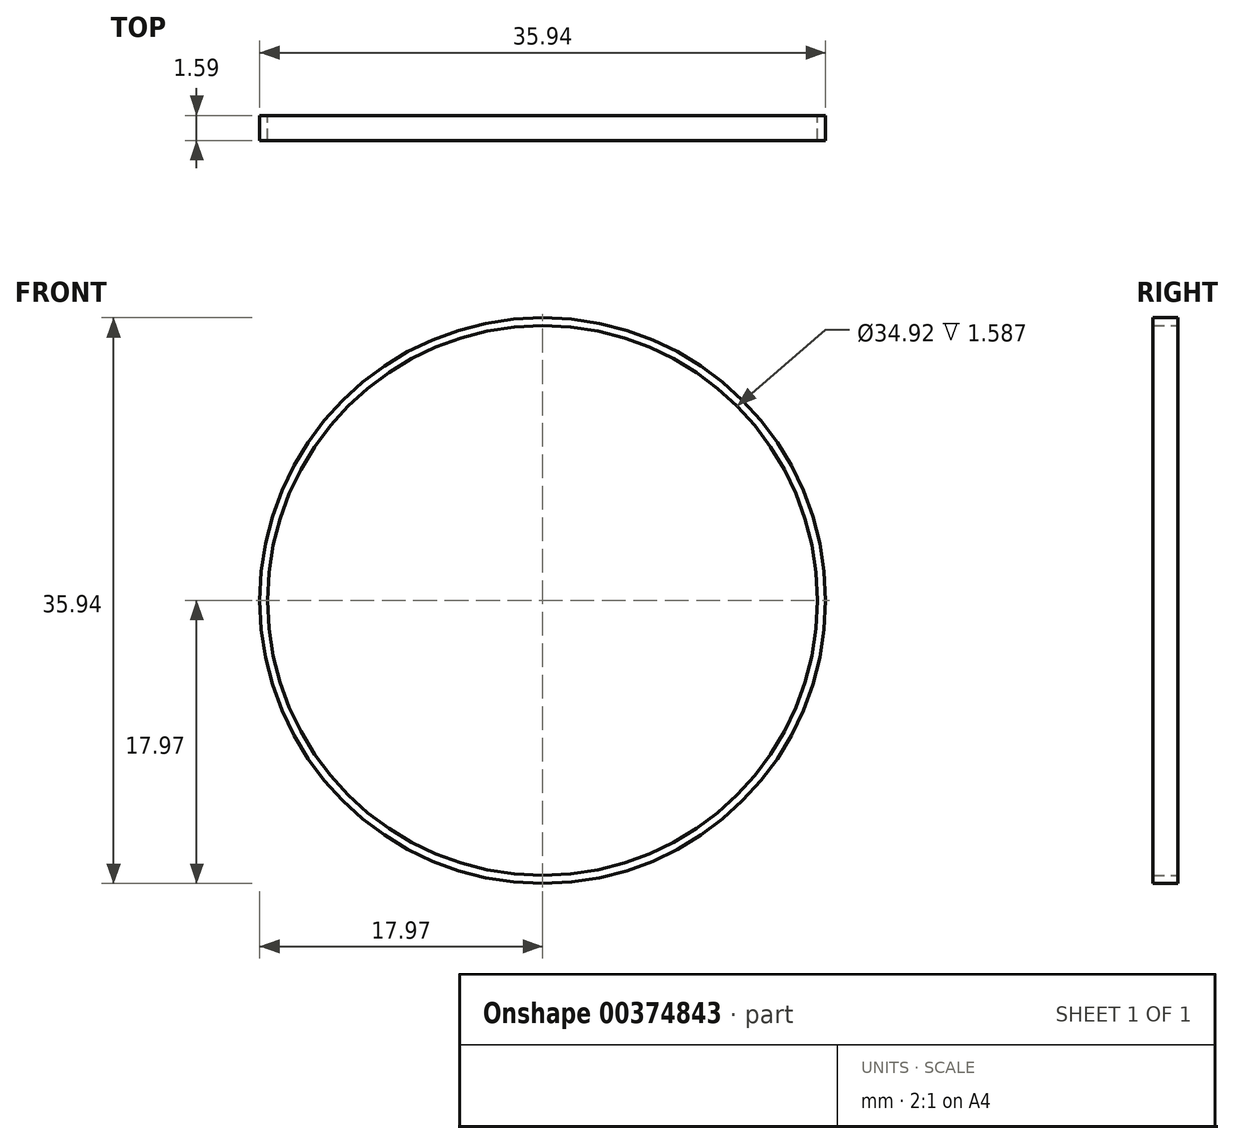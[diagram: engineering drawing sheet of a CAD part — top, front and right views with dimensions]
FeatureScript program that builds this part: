
annotation { "Feature Type Name" : "Feature", "Feature Type Description" : "" }
export const myFeature = defineFeature(function(context is Context, id is Id, definition is map)
    precondition{}
    {
        {
            var Q0;
            Q0=qCreatedBy(makeId("Front.planeOp"),FACE);
            var sketch = newSketch(context, id + "F0", { "sketchPlane" : qUnion([Q0])});
            skCircle(sketch, "E0", {"center": v(0, 0) * mm, "radius": 17.97 * mm});
            skCircle(sketch, "E1", {"center": v(0, 0) * mm, "radius": 17.46 * mm});
            skSolve(sketch);
        }
        {
            var Q0;
            Q0=makeQuery(id+"F0.imprint","IMPRINT",FACE,{"disambiguationData":[TD([[makeQuery(id+"F0.imprint","IMPRINT",EDGE,{"derivedFrom":sQuery(id+"F0.wireOp",EDGE,"E0")}),1.0]])]});
            extrude(context, id + "F1", {"entities" : qUnion([Q0]), "depth" : 1.59 * mm});
        }
    });
